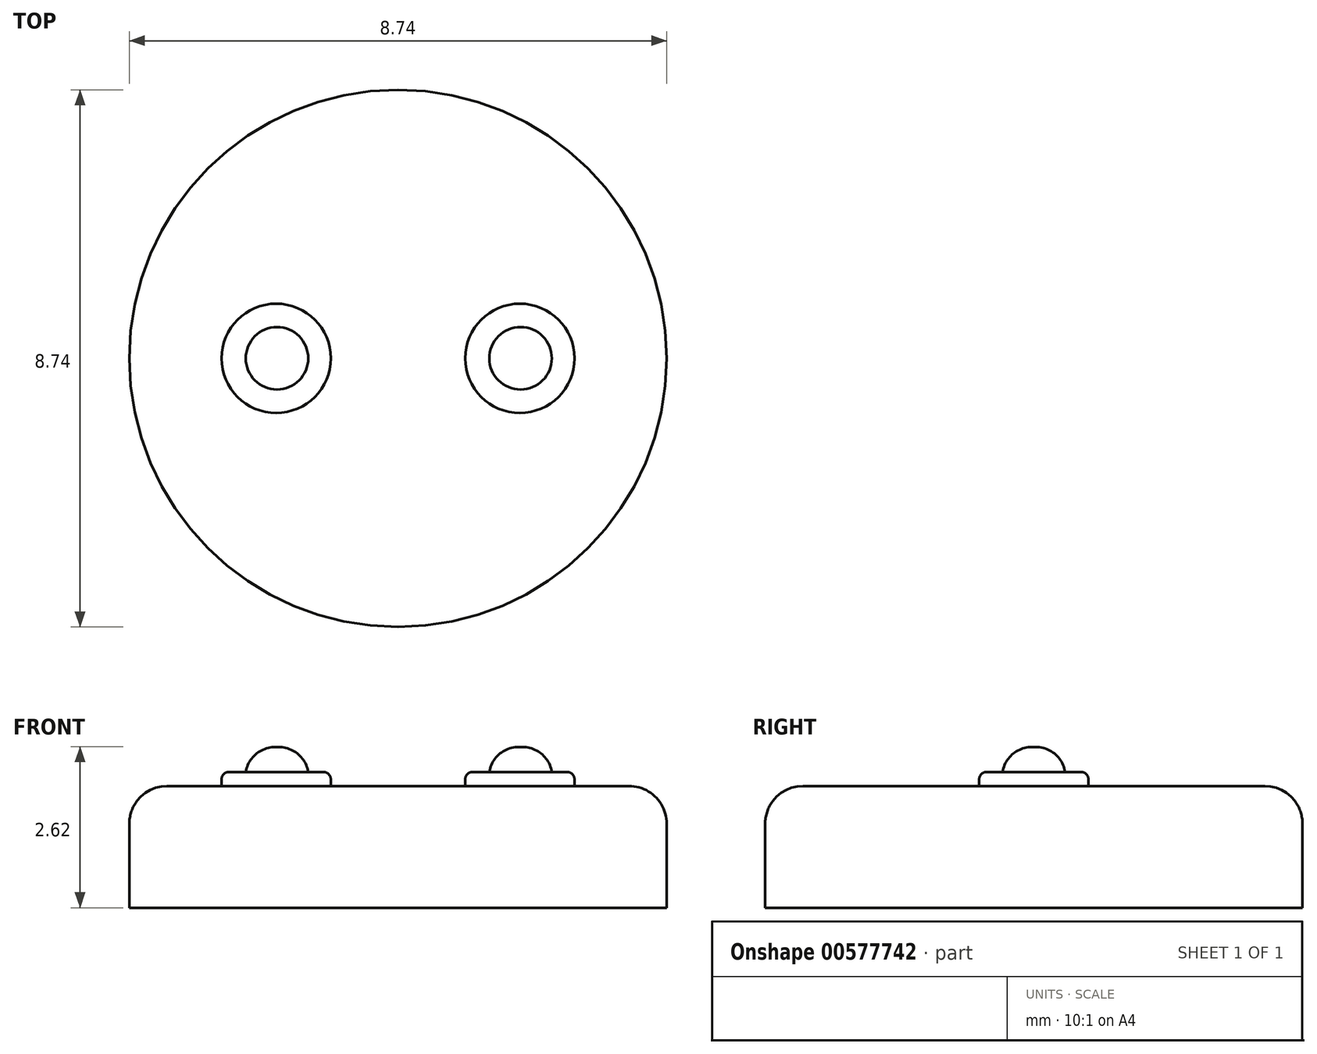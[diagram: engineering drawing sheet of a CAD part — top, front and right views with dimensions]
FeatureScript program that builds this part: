
annotation { "Feature Type Name" : "Feature", "Feature Type Description" : "" }
export const myFeature = defineFeature(function(context is Context, id is Id, definition is map)
    precondition{}
    {
        {
            var Q0;
            Q0=qCreatedBy(makeId("Top.planeOp"),FACE);
            var sketch = newSketch(context, id + "F0", { "sketchPlane" : qUnion([Q0])});
            skCircle(sketch, "E0", {"center": v(0, 0) * mm, "radius": 4.37 * mm});
            skSolve(sketch);
        }
        {
            var Q0;
            Q0=makeQuery(id+"F0.imprint","IMPRINT",FACE,{"disambiguationData":[TD([[makeQuery(id+"F0.imprint","IMPRINT",EDGE,{"derivedFrom":sQuery(id+"F0.wireOp",EDGE,"E0")}),1.0]])]});
            extrude(context, id + "F1", {"entities" : qUnion([Q0]), "depth" : 1.98 * mm, "offsetDistance" : 25.4 * mm});
        }
        {
            var Q0;
            Q0=qCreatedBy(makeId("Top.planeOp"),FACE);
            var sketch = newSketch(context, id + "F2", { "sketchPlane" : qUnion([Q0])});
            skCircle(sketch, "E1", {"center": v(-1.98, 0) * mm, "radius": 0.89 * mm});
            skCircle(sketch, "E2", {"center": v(1.98, 0) * mm, "radius": 0.89 * mm});
            skSolve(sketch);
        }
        {
            var Q0;
            Q0=makeQuery(id+"F2.imprint","IMPRINT",FACE,{"disambiguationData":[TD([[makeQuery(id+"F2.imprint","IMPRINT",EDGE,{"derivedFrom":sQuery(id+"F2.wireOp",EDGE,"E1")}),1.0]])]});
            var Q1;
            Q1=makeQuery(id+"F2.imprint","IMPRINT",FACE,{"disambiguationData":[TD([[makeQuery(id+"F2.imprint","IMPRINT",EDGE,{"derivedFrom":sQuery(id+"F2.wireOp",EDGE,"E2")}),1.0]])]});
            extrude(context, id + "F3", {"entities" : qUnion([Q0, Q1]), "operationType" : NewBodyOperationType.ADD, "depth" : 2.2 * mm, "offsetDistance" : 25.4 * mm});
        }
        {
            var Q0;
            Q0=qCreatedBy(makeId("Top.planeOp"),FACE);
            var sketch = newSketch(context, id + "F4", { "sketchPlane" : qUnion([Q0])});
            skCircle(sketch, "E3", {"center": v(-1.97, 0) * mm, "radius": 0.5 * mm});
            skCircle(sketch, "E4", {"center": v(2, 0) * mm, "radius": 0.5 * mm});
            skSolve(sketch);
        }
        {
            var Q0;
            Q0=makeQuery(id+"F4.imprint","IMPRINT",FACE,{"disambiguationData":[TD([[makeQuery(id+"F4.imprint","IMPRINT",EDGE,{"derivedFrom":sQuery(id+"F4.wireOp",EDGE,"E3")}),1.0]])]});
            var Q1;
            Q1=makeQuery(id+"F4.imprint","IMPRINT",FACE,{"disambiguationData":[TD([[makeQuery(id+"F4.imprint","IMPRINT",EDGE,{"derivedFrom":sQuery(id+"F4.wireOp",EDGE,"E4")}),1.0]])]});
            extrude(context, id + "F5", {"entities" : qUnion([Q0, Q1]), "operationType" : NewBodyOperationType.ADD, "depth" : 2.62 * mm, "offsetDistance" : 25.4 * mm});
        }
        {
            var Q0;
            Q0=makeQuery(id+"F5.opExtrude","CAP_EDGE",EDGE,{"disambiguationData":[OSD([sQuery(id+"F4.wireOp",EDGE,"E3")])],"isStart":false});
            fillet(context, id + "F6", {"entities" : qUnion([Q0]), "radius" : 0.5 * mm, "tangentPropagation" : true, "allowEdgeOverflow" : false});
        }
        {
            var Q0;
            Q0=makeQuery(id+"F5.opExtrude","CAP_EDGE",EDGE,{"disambiguationData":[OSD([sQuery(id+"F4.wireOp",EDGE,"E4")])],"isStart":false});
            fillet(context, id + "F7", {"entities" : qUnion([Q0]), "radius" : 0.48 * mm, "tangentPropagation" : true, "allowEdgeOverflow" : false});
        }
        {
            var Q0;
            Q0=makeQuery(id+"F3.opExtrude","CAP_EDGE",EDGE,{"disambiguationData":[OSD([sQuery(id+"F2.wireOp",EDGE,"E1")])],"isStart":false});
            var Q1;
            Q1=makeQuery(id+"F3.opExtrude","CAP_EDGE",EDGE,{"disambiguationData":[OSD([sQuery(id+"F2.wireOp",EDGE,"E2")])],"isStart":false});
            fillet(context, id + "F8", {"entities" : qUnion([Q0, Q1]), "radius" : 0.12 * mm, "tangentPropagation" : true, "allowEdgeOverflow" : false});
        }
        {
            var Q0;
            Q0=makeQuery(id+"F1.opExtrude","CAP_EDGE",EDGE,{"disambiguationData":[OSD([sQuery(id+"F0.wireOp",EDGE,"E0")])],"isStart":false});
            fillet(context, id + "F9", {"entities" : qUnion([Q0]), "radius" : 0.61 * mm, "tangentPropagation" : true, "allowEdgeOverflow" : false});
        }
    });
